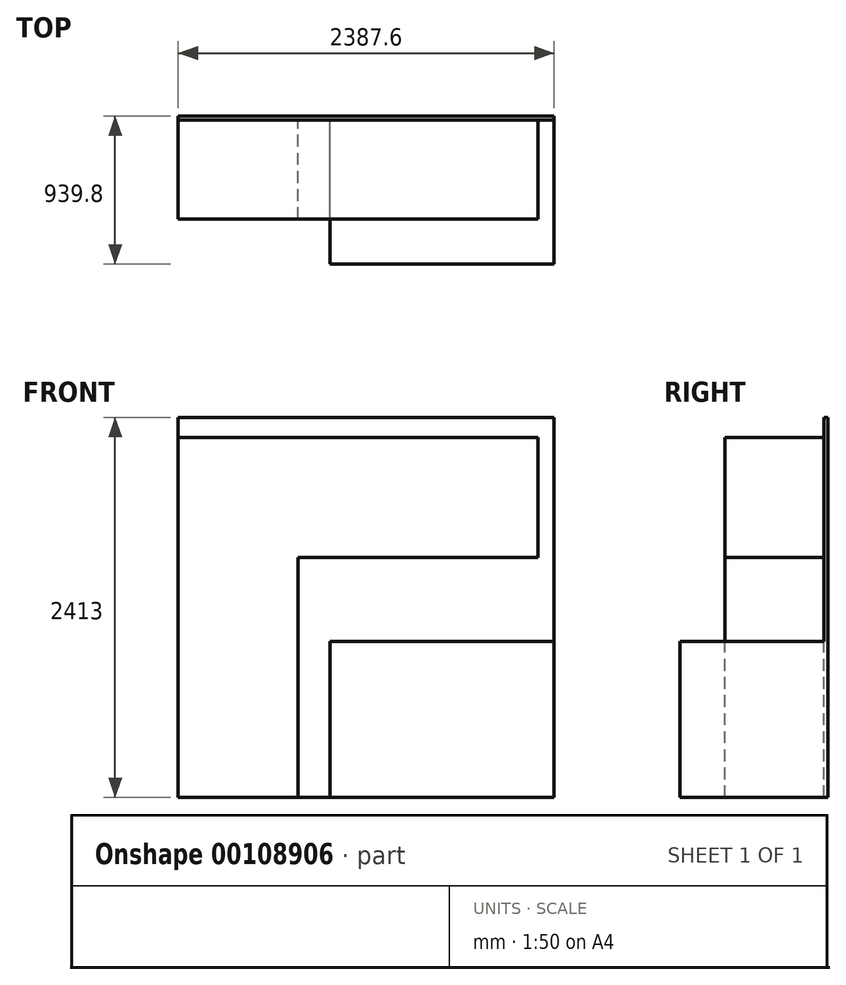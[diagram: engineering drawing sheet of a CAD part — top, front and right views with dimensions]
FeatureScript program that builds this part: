
annotation { "Feature Type Name" : "Feature", "Feature Type Description" : "" }
export const myFeature = defineFeature(function(context is Context, id is Id, definition is map)
    precondition{}
    {
        {
            var Q0;
            Q0=qCreatedBy(makeId("Front.planeOp"),FACE);
            var sketch = newSketch(context, id + "F0", { "sketchPlane" : qUnion([Q0])});
            skLineSegment(sketch, "E0.bottom", {"start": v(-1193.8, -1206.5) * mm, "end": v(1193.8, -1206.5) * mm});
            skLineSegment(sketch, "E0.top", {"start": v(-1193.8, 1206.5) * mm, "end": v(1193.8, 1206.5) * mm});
            skLineSegment(sketch, "E0.left", {"start": v(-1193.8, -1206.5) * mm, "end": v(-1193.8, 1206.5) * mm});
            skLineSegment(sketch, "E0.right", {"start": v(1193.8, -1206.5) * mm, "end": v(1193.8, 1206.5) * mm});
            skPoint(sketch, "E0.middle", {"position": v(0, 0) * mm});
            skSolve(sketch);
        }
        {
            var Q0;
            Q0 = qSketchRegion(id + "F0", true);
            extrude(context, id + "F1", {"entities" : qUnion([Q0]), "depth" : 25.4 * mm});
        }
        {
            var Q0;
            Q0=makeQuery(id+"F1.opExtrude","CAP_FACE",FACE,{"disambiguationData":[OSD([sQuery(id+"F0.wireOp",EDGE,"E0.bottom"),sQuery(id+"F0.wireOp",EDGE,"E0.top"),sQuery(id+"F0.wireOp",EDGE,"E0.left"),sQuery(id+"F0.wireOp",EDGE,"E0.right")])],"isStart":false});
            var sketch = newSketch(context, id + "F2", { "sketchPlane" : qUnion([Q0])});
            skLineSegment(sketch, "E1.bottom", {"start": v(1193.8, -1206.5) * mm, "end": v(-228.6, -1206.5) * mm});
            skLineSegment(sketch, "E1.top", {"start": v(1193.8, -215.9) * mm, "end": v(-228.6, -215.9) * mm});
            skLineSegment(sketch, "E1.left", {"start": v(1193.8, -1206.5) * mm, "end": v(1193.8, -215.9) * mm});
            skLineSegment(sketch, "E1.right", {"start": v(-228.6, -1206.5) * mm, "end": v(-228.6, -215.9) * mm});
            skSolve(sketch);
        }
        {
            var Q0;
            Q0 = qSketchRegion(id + "F2", true);
            extrude(context, id + "F3", {"entities" : qUnion([Q0]), "operationType" : NewBodyOperationType.ADD, "depth" : 914.4 * mm});
        }
        {
            var Q0;
            Q0=makeQuery(id+"F1.opExtrude","CAP_FACE",FACE,{"disambiguationData":[OSD([sQuery(id+"F0.wireOp",EDGE,"E0.bottom"),sQuery(id+"F0.wireOp",EDGE,"E0.top"),sQuery(id+"F0.wireOp",EDGE,"E0.left"),sQuery(id+"F0.wireOp",EDGE,"E0.right")])],"isStart":false});
            var sketch = newSketch(context, id + "F4", { "sketchPlane" : qUnion([Q0])});
            skLineSegment(sketch, "E2.bottom", {"start": v(-1193.8, -1206.5) * mm, "end": v(-431.8, -1206.5) * mm});
            skLineSegment(sketch, "E2.top", {"start": v(-1193.8, 1079.5) * mm, "end": v(-431.8, 1079.5) * mm});
            skLineSegment(sketch, "E2.left", {"start": v(-1193.8, -1206.5) * mm, "end": v(-1193.8, 1079.5) * mm});
            skLineSegment(sketch, "E2.right", {"start": v(-431.8, -1206.5) * mm, "end": v(-431.8, 1079.5) * mm});
            skLineSegment(sketch, "E3.bottom", {"start": v(-431.8, 1079.5) * mm, "end": v(330.2, 1079.5) * mm});
            skLineSegment(sketch, "E3.top", {"start": v(-431.8, 317.5) * mm, "end": v(330.2, 317.5) * mm});
            skLineSegment(sketch, "E3.left", {"start": v(-431.8, 1079.5) * mm, "end": v(-431.8, 317.5) * mm});
            skLineSegment(sketch, "E3.right", {"start": v(330.2, 1079.5) * mm, "end": v(330.2, 317.5) * mm});
            skLineSegment(sketch, "E4.bottom", {"start": v(330.2, 1079.5) * mm, "end": v(1092.2, 1079.5) * mm});
            skLineSegment(sketch, "E4.top", {"start": v(330.2, 317.5) * mm, "end": v(1092.2, 317.5) * mm});
            skLineSegment(sketch, "E4.right", {"start": v(1092.2, 1079.5) * mm, "end": v(1092.2, 317.5) * mm});
            skSolve(sketch);
        }
        {
            var Q0;
            Q0 = qSketchRegion(id + "F4", true);
            extrude(context, id + "F5", {"entities" : qUnion([Q0]), "operationType" : NewBodyOperationType.ADD, "depth" : 628.65 * mm});
        }
    });
